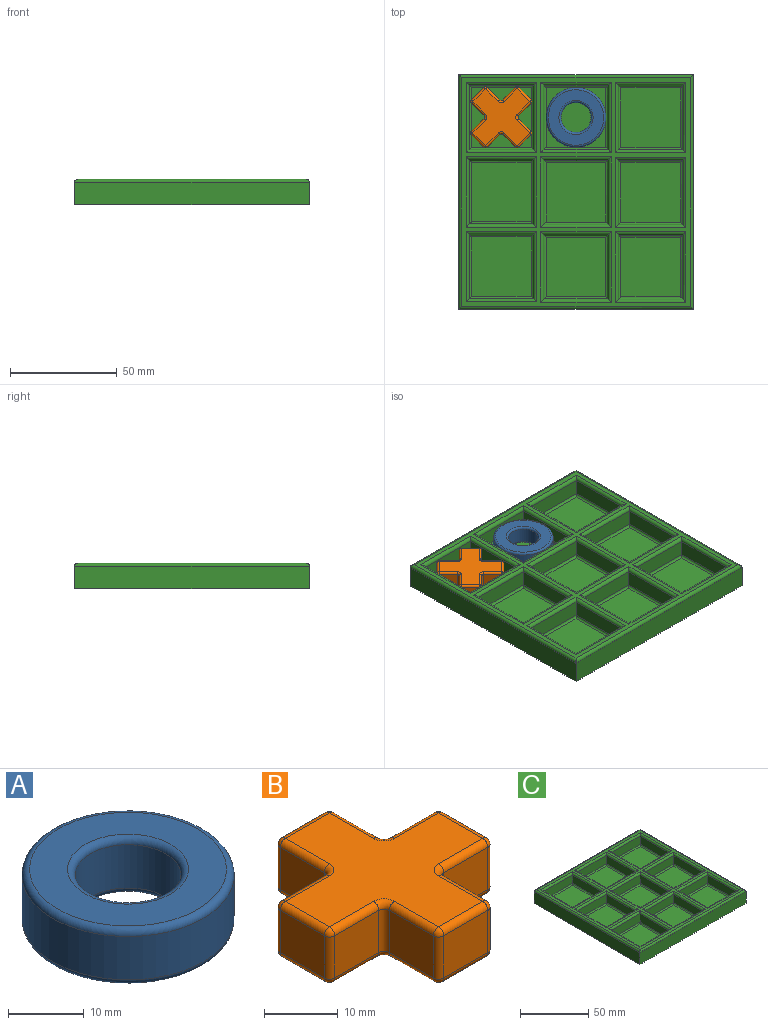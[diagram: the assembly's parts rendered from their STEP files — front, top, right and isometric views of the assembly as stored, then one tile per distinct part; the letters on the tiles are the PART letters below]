
ASSEMBLY  parts=3 mates=2
PART A: 8 faces, bbox 30.3x30.3x9 mm
  f0: cylinder r=7mm len=14mm, axis (0,0,-1), area 307.9mm2, adj f4,f6
  f1: cylinder r=14mm len=28mm, axis (0,0,-1), area 615.8mm2, adj f5,f7
  f2: plane 26x26mm, normal (0,0,1), area 329.9mm2, adj f6,f7
  f3: plane 26x26mm, normal (0,0,-1), area 329.9mm2, adj f4,f5
  f4: torus R=8mm, axis (0,0,1), area 72.7mm2, adj f0,f3
  f5: torus R=13mm, axis (0,0,1), area 134.6mm2, adj f1,f3
  f6: torus R=8mm, axis (0,0,1), area 72.7mm2, adj f0,f2
  f7: torus R=13mm, axis (0,0,1), area 134.6mm2, adj f1,f2
PART B: 74 faces, bbox 31.3x31.3x9 mm
  f0: plane 8.44x7mm, normal (-1,0,0), area 59mm2, adj f62,f67,f70,f73
  f1: plane 8.44x7mm, normal (0,-1,0), area 59mm2, adj f59,f68,f69,f73
  f2: plane 8.44x7mm, normal (1,0,0), area 59mm2, adj f49,f58,f59,f60
  f3: plane 8.44x7mm, normal (0,-1,0), area 59mm2, adj f39,f48,f49,f50
  f4: plane 8.44x7mm, normal (1,0,0), area 59mm2, adj f29,f38,f39,f40
  f5: plane 8.44x7mm, normal (0,1,0), area 59mm2, adj f19,f28,f29,f30
  f6: plane 8.44x7mm, normal (1,0,0), area 59mm2, adj f14,f18,f19,f20
  f7: plane 8.44x7mm, normal (0,1,0), area 59mm2, adj f14,f17,f21,f22
  f8: plane 8.44x7mm, normal (-1,0,0), area 59mm2, adj f22,f27,f31,f32
  f9: plane 8.44x7mm, normal (0,1,0), area 59mm2, adj f32,f37,f41,f42
  f10: plane 8.44x7mm, normal (-1,0,0), area 59mm2, adj f42,f47,f51,f52
  f11: plane 8.44x7mm, normal (0,-1,0), area 59mm2, adj f52,f57,f61,f62
  f12: plane 29.31x29.31mm, normal (0,0,1), area 426.7mm2, adj f17,f18,f24,f27,f28,f33,f37,f38
  f13: plane 29.31x29.31mm, normal (0,0,-1), area 426.7mm2, adj f20,f21,f25,f30,f31,f36,f40,f41
  f14: cylinder r=1mm len=7mm, axis (0,0,1), area 11mm2, adj f6,f7,f15,f16
  f15: sphere r=1mm, area 1.6mm2, adj f14,f17,f18
  f16: sphere r=1mm, area 1.6mm2, adj f14,f20,f21
  f17: cylinder r=1mm len=8.44mm, axis (1,0,0), area 13.3mm2, adj f7,f12,f15,f23
  f18: cylinder r=1mm len=8.44mm, axis (0,-1,0), area 13.3mm2, adj f6,f12,f15,f24
  f19: cylinder r=1mm len=7mm, axis (0,0,-1), area 11mm2, adj f5,f6,f24,f25
  f20: cylinder r=1mm len=8.44mm, axis (0,1,0), area 13.3mm2, adj f6,f13,f16,f25
  f21: cylinder r=1mm len=8.44mm, axis (-1,0,0), area 13.3mm2, adj f7,f13,f16,f26
  f22: cylinder r=1mm len=7mm, axis (0,0,1), area 11mm2, adj f7,f8,f23,f26
  f23: sphere r=1mm, area 1.6mm2, adj f17,f22,f27
  f24: torus R=2mm, axis (0,0,1), area 3.4mm2, adj f12,f18,f19,f28
  f25: torus R=2mm, axis (0,0,1), area 3.4mm2, adj f13,f19,f20,f30
  f26: sphere r=1mm, area 1.6mm2, adj f21,f22,f31
  f27: cylinder r=1mm len=8.44mm, axis (0,1,0), area 13.3mm2, adj f8,f12,f23,f33
  f28: cylinder r=1mm len=8.44mm, axis (1,0,0), area 13.3mm2, adj f5,f12,f24,f34
  f29: cylinder r=1mm len=7mm, axis (0,0,-1), area 11mm2, adj f4,f5,f34,f35
  f30: cylinder r=1mm len=8.44mm, axis (-1,0,0), area 13.3mm2, adj f5,f13,f25,f35
  f31: cylinder r=1mm len=8.44mm, axis (0,-1,0), area 13.3mm2, adj f8,f13,f26,f36
  f32: cylinder r=1mm len=7mm, axis (0,0,-1), area 11mm2, adj f8,f9,f33,f36
  f33: torus R=2mm, axis (0,0,1), area 3.4mm2, adj f12,f27,f32,f37
  f34: sphere r=1mm, area 1.6mm2, adj f28,f29,f38
  f35: sphere r=1mm, area 1.6mm2, adj f29,f30,f40
  f36: torus R=2mm, axis (0,0,1), area 3.4mm2, adj f13,f31,f32,f41
  f37: cylinder r=1mm len=8.44mm, axis (1,0,0), area 13.3mm2, adj f9,f12,f33,f43
  f38: cylinder r=1mm len=8.44mm, axis (0,-1,0), area 13.3mm2, adj f4,f12,f34,f44
  f39: cylinder r=1mm len=7mm, axis (0,0,1), area 11mm2, adj f3,f4,f44,f45
  f40: cylinder r=1mm len=8.44mm, axis (0,1,0), area 13.3mm2, adj f4,f13,f35,f45
  f41: cylinder r=1mm len=8.44mm, axis (-1,0,0), area 13.3mm2, adj f9,f13,f36,f46
  f42: cylinder r=1mm len=7mm, axis (0,0,1), area 11mm2, adj f9,f10,f43,f46
  f43: sphere r=1mm, area 1.6mm2, adj f37,f42,f47
  f44: sphere r=1mm, area 1.6mm2, adj f38,f39,f48
  f45: sphere r=1mm, area 1.6mm2, adj f39,f40,f50
  f46: sphere r=1mm, area 1.6mm2, adj f41,f42,f51
  f47: cylinder r=1mm len=8.44mm, axis (0,1,0), area 13.3mm2, adj f10,f12,f43,f53
  f48: cylinder r=1mm len=8.44mm, axis (-1,0,0), area 13.3mm2, adj f3,f12,f44,f54
  f49: cylinder r=1mm len=7mm, axis (0,0,1), area 11mm2, adj f2,f3,f54,f55
  f50: cylinder r=1mm len=8.44mm, axis (1,0,0), area 13.3mm2, adj f3,f13,f45,f55
  f51: cylinder r=1mm len=8.44mm, axis (0,-1,0), area 13.3mm2, adj f10,f13,f46,f56
  f52: cylinder r=1mm len=7mm, axis (0,0,-1), area 11mm2, adj f10,f11,f53,f56
  f53: sphere r=1mm, area 1.6mm2, adj f47,f52,f57
  f54: torus R=2mm, axis (0,0,1), area 3.4mm2, adj f12,f48,f49,f58
  f55: torus R=2mm, axis (0,0,1), area 3.4mm2, adj f13,f49,f50,f60
  f56: sphere r=1mm, area 1.6mm2, adj f51,f52,f61
  f57: cylinder r=1mm len=8.44mm, axis (-1,0,0), area 13.3mm2, adj f11,f12,f53,f63
  f58: cylinder r=1mm len=8.44mm, axis (0,-1,0), area 13.3mm2, adj f2,f12,f54,f64
  f59: cylinder r=1mm len=7mm, axis (0,0,-1), area 11mm2, adj f1,f2,f64,f65
  f60: cylinder r=1mm len=8.44mm, axis (0,1,0), area 13.3mm2, adj f2,f13,f55,f65
  f61: cylinder r=1mm len=8.44mm, axis (1,0,0), area 13.3mm2, adj f11,f13,f56,f66
  f62: cylinder r=1mm len=7mm, axis (0,0,1), area 11mm2, adj f0,f11,f63,f66
  f63: torus R=2mm, axis (0,0,1), area 3.4mm2, adj f12,f57,f62,f67
  f64: sphere r=1mm, area 1.6mm2, adj f58,f59,f68
  f65: sphere r=1mm, area 1.6mm2, adj f59,f60,f69
  f66: torus R=2mm, axis (0,0,1), area 3.4mm2, adj f13,f61,f62,f70
  f67: cylinder r=1mm len=8.44mm, axis (0,1,0), area 13.3mm2, adj f0,f12,f63,f71
  f68: cylinder r=1mm len=8.44mm, axis (-1,0,0), area 13.3mm2, adj f1,f12,f64,f71
  f69: cylinder r=1mm len=8.44mm, axis (1,0,0), area 13.3mm2, adj f1,f13,f65,f72
  f70: cylinder r=1mm len=8.44mm, axis (0,-1,0), area 13.3mm2, adj f0,f13,f66,f72
  f71: sphere r=1mm, area 1.6mm2, adj f67,f68,f73
  f72: sphere r=1mm, area 1.6mm2, adj f69,f70,f73
  f73: cylinder r=1mm len=7mm, axis (0,0,-1), area 11mm2, adj f0,f1,f71,f72
PART C: 127 faces, bbox 110x110x12 mm
  f0: plane 107x107mm, normal (0,0,1), area 1648mm2, adj f51,f52,f53,f54,f55,f56,f57,f58
  f1: plane 110x10.5mm, normal (0,1,0), area 1155mm2, adj f2,f4,f5,f87
  f2: plane 110x10.5mm, normal (-1,0,0), area 1155mm2, adj f1,f3,f5,f88
  f3: plane 110x10.5mm, normal (0,-1,0), area 1155mm2, adj f2,f4,f5,f90
  f4: plane 110x10.5mm, normal (1,0,0), area 1155mm2, adj f1,f3,f5,f89
  f5: plane 110x110mm, normal (0,0,-1), area 12100mm2, adj f1,f2,f3,f4
  f6: plane 30x7.5mm, normal (0,-1,0), area 225mm2, adj f7,f9,f84,f124
  f7: plane 30x7.5mm, normal (1,0,0), area 225mm2, adj f6,f8,f86,f126
  f8: plane 30x7.5mm, normal (0,1,0), area 225mm2, adj f7,f9,f85,f125
  f9: plane 30x7.5mm, normal (-1,0,0), area 225mm2, adj f6,f8,f83,f123
  f10: plane 28x28mm, normal (0,0,1), area 784mm2, adj f123,f124,f125,f126
  f11: plane 30x7.5mm, normal (0,-1,0), area 225mm2, adj f12,f14,f64,f104
  f12: plane 30x7.5mm, normal (1,0,0), area 225mm2, adj f11,f13,f66,f106
  f13: plane 30x7.5mm, normal (0,1,0), area 225mm2, adj f12,f14,f65,f105
  f14: plane 30x7.5mm, normal (-1,0,0), area 225mm2, adj f11,f13,f63,f103
  f15: plane 28x28mm, normal (0,0,1), area 784mm2, adj f103,f104,f105,f106
  f16: plane 30x7.5mm, normal (0,-1,0), area 225mm2, adj f17,f19,f60,f100
  f17: plane 30x7.5mm, normal (1,0,0), area 225mm2, adj f16,f18,f62,f102
  f18: plane 30x7.5mm, normal (0,1,0), area 225mm2, adj f17,f19,f61,f101
  f19: plane 30x7.5mm, normal (-1,0,0), area 225mm2, adj f16,f18,f59,f99
  f20: plane 28x28mm, normal (0,0,1), area 784mm2, adj f99,f100,f101,f102
  f21: plane 30x7.5mm, normal (0,-1,0), area 225mm2, adj f22,f24,f56,f96
  f22: plane 30x7.5mm, normal (1,0,0), area 225mm2, adj f21,f23,f58,f98
  f23: plane 30x7.5mm, normal (0,1,0), area 225mm2, adj f22,f24,f57,f97
  f24: plane 30x7.5mm, normal (-1,0,0), area 225mm2, adj f21,f23,f55,f95
  f25: plane 28x28mm, normal (0,0,1), area 784mm2, adj f95,f96,f97,f98
  f26: plane 30x7.5mm, normal (0,-1,0), area 225mm2, adj f27,f29,f52,f92
  f27: plane 30x7.5mm, normal (1,0,0), area 225mm2, adj f26,f28,f54,f94
  f28: plane 30x7.5mm, normal (0,1,0), area 225mm2, adj f27,f29,f53,f93
  f29: plane 30x7.5mm, normal (-1,0,0), area 225mm2, adj f26,f28,f51,f91
  f30: plane 28x28mm, normal (0,0,1), area 784mm2, adj f91,f92,f93,f94
  f31: plane 30x7.5mm, normal (0,-1,0), area 225mm2, adj f32,f34,f68,f108
  f32: plane 30x7.5mm, normal (1,0,0), area 225mm2, adj f31,f33,f70,f110
  f33: plane 30x7.5mm, normal (0,1,0), area 225mm2, adj f32,f34,f69,f109
  f34: plane 30x7.5mm, normal (-1,0,0), area 225mm2, adj f31,f33,f67,f107
  f35: plane 28x28mm, normal (0,0,1), area 784mm2, adj f107,f108,f109,f110
  f36: plane 30x7.5mm, normal (0,-1,0), area 225mm2, adj f37,f39,f72,f112
  f37: plane 30x7.5mm, normal (1,0,0), area 225mm2, adj f36,f38,f74,f114
  f38: plane 30x7.5mm, normal (0,1,0), area 225mm2, adj f37,f39,f73,f113
  f39: plane 30x7.5mm, normal (-1,0,0), area 225mm2, adj f36,f38,f71,f111
  f40: plane 28x28mm, normal (0,0,1), area 784mm2, adj f111,f112,f113,f114
  f41: plane 30x7.5mm, normal (0,-1,0), area 225mm2, adj f42,f44,f76,f116
  f42: plane 30x7.5mm, normal (1,0,0), area 225mm2, adj f41,f43,f78,f118
  f43: plane 30x7.5mm, normal (0,1,0), area 225mm2, adj f42,f44,f77,f117
  f44: plane 30x7.5mm, normal (-1,0,0), area 225mm2, adj f41,f43,f75,f115
  f45: plane 28x28mm, normal (0,0,1), area 784mm2, adj f115,f116,f117,f118
  f46: plane 30x7.5mm, normal (0,-1,0), area 225mm2, adj f47,f49,f79,f119
  f47: plane 30x7.5mm, normal (1,0,0), area 225mm2, adj f46,f48,f80,f120
  f48: plane 30x7.5mm, normal (0,1,0), area 225mm2, adj f47,f49,f82,f122
  f49: plane 30x7.5mm, normal (-1,0,0), area 225mm2, adj f46,f48,f81,f121
  f50: plane 28x28mm, normal (0,0,1), area 784mm2, adj f119,f120,f121,f122
  f51: cylinder r=1.5mm len=33mm, axis (0,-1,0), area 73.3mm2, adj f0,f29,f52,f53
  f52: cylinder r=1.5mm len=33mm, axis (1,0,0), area 73.3mm2, adj f0,f26,f51,f54
  f53: cylinder r=1.5mm len=33mm, axis (-1,0,0), area 73.3mm2, adj f0,f28,f51,f54
  f54: cylinder r=1.5mm len=33mm, axis (0,1,0), area 73.3mm2, adj f0,f27,f52,f53
  f55: cylinder r=1.5mm len=33mm, axis (0,-1,0), area 73.3mm2, adj f0,f24,f56,f57
  f56: cylinder r=1.5mm len=33mm, axis (1,0,0), area 73.3mm2, adj f0,f21,f55,f58
  f57: cylinder r=1.5mm len=33mm, axis (-1,0,0), area 73.3mm2, adj f0,f23,f55,f58
  f58: cylinder r=1.5mm len=33mm, axis (0,1,0), area 73.3mm2, adj f0,f22,f56,f57
  f59: cylinder r=1.5mm len=33mm, axis (0,-1,0), area 73.3mm2, adj f0,f19,f60,f61
  f60: cylinder r=1.5mm len=33mm, axis (1,0,0), area 73.3mm2, adj f0,f16,f59,f62
  f61: cylinder r=1.5mm len=33mm, axis (-1,0,0), area 73.3mm2, adj f0,f18,f59,f62
  f62: cylinder r=1.5mm len=33mm, axis (0,1,0), area 73.3mm2, adj f0,f17,f60,f61
  f63: cylinder r=1.5mm len=33mm, axis (0,-1,0), area 73.3mm2, adj f0,f14,f64,f65
  f64: cylinder r=1.5mm len=33mm, axis (1,0,0), area 73.3mm2, adj f0,f11,f63,f66
  f65: cylinder r=1.5mm len=33mm, axis (-1,0,0), area 73.3mm2, adj f0,f13,f63,f66
  f66: cylinder r=1.5mm len=33mm, axis (0,1,0), area 73.3mm2, adj f0,f12,f64,f65
  f67: cylinder r=1.5mm len=33mm, axis (0,-1,0), area 73.3mm2, adj f0,f34,f68,f69
  f68: cylinder r=1.5mm len=33mm, axis (1,0,0), area 73.3mm2, adj f0,f31,f67,f70
  f69: cylinder r=1.5mm len=33mm, axis (-1,0,0), area 73.3mm2, adj f0,f33,f67,f70
  f70: cylinder r=1.5mm len=33mm, axis (0,1,0), area 73.3mm2, adj f0,f32,f68,f69
  f71: cylinder r=1.5mm len=33mm, axis (0,-1,0), area 73.3mm2, adj f0,f39,f72,f73
  f72: cylinder r=1.5mm len=33mm, axis (1,0,0), area 73.3mm2, adj f0,f36,f71,f74
  f73: cylinder r=1.5mm len=33mm, axis (-1,0,0), area 73.3mm2, adj f0,f38,f71,f74
  f74: cylinder r=1.5mm len=33mm, axis (0,1,0), area 73.3mm2, adj f0,f37,f72,f73
  f75: cylinder r=1.5mm len=33mm, axis (0,-1,0), area 73.3mm2, adj f0,f44,f76,f77
  f76: cylinder r=1.5mm len=33mm, axis (1,0,0), area 73.3mm2, adj f0,f41,f75,f78
  f77: cylinder r=1.5mm len=33mm, axis (-1,0,0), area 73.3mm2, adj f0,f43,f75,f78
  f78: cylinder r=1.5mm len=33mm, axis (0,1,0), area 73.3mm2, adj f0,f42,f76,f77
  f79: cylinder r=1.5mm len=33mm, axis (1,0,0), area 73.3mm2, adj f0,f46,f80,f81
  f80: cylinder r=1.5mm len=33mm, axis (0,1,0), area 73.3mm2, adj f0,f47,f79,f82
  f81: cylinder r=1.5mm len=33mm, axis (0,-1,0), area 73.3mm2, adj f0,f49,f79,f82
  f82: cylinder r=1.5mm len=33mm, axis (-1,0,0), area 73.3mm2, adj f0,f48,f80,f81
  f83: cylinder r=1.5mm len=33mm, axis (0,-1,0), area 73.3mm2, adj f0,f9,f84,f85
  f84: cylinder r=1.5mm len=33mm, axis (1,0,0), area 73.3mm2, adj f0,f6,f83,f86
  f85: cylinder r=1.5mm len=33mm, axis (-1,0,0), area 73.3mm2, adj f0,f8,f83,f86
  f86: cylinder r=1.5mm len=33mm, axis (0,1,0), area 73.3mm2, adj f0,f7,f84,f85
  f87: cylinder r=1.5mm len=110mm, axis (1,0,0), area 256.6mm2, adj f0,f1,f88,f89
  f88: cylinder r=1.5mm len=110mm, axis (0,1,0), area 256.6mm2, adj f0,f2,f87,f90
  f89: cylinder r=1.5mm len=110mm, axis (0,-1,0), area 256.6mm2, adj f0,f4,f87,f90
  f90: cylinder r=1.5mm len=110mm, axis (-1,0,0), area 256.6mm2, adj f0,f3,f88,f89
  f91: cylinder r=1mm len=30mm, axis (0,1,0), area 46mm2, adj f29,f30,f92,f93
  f92: cylinder r=1mm len=30mm, axis (-1,0,0), area 46mm2, adj f26,f30,f91,f94
  f93: cylinder r=1mm len=30mm, axis (1,0,0), area 46mm2, adj f28,f30,f91,f94
  f94: cylinder r=1mm len=30mm, axis (0,-1,0), area 46mm2, adj f27,f30,f92,f93
  f95: cylinder r=1mm len=30mm, axis (0,1,0), area 46mm2, adj f24,f25,f96,f97
  f96: cylinder r=1mm len=30mm, axis (-1,0,0), area 46mm2, adj f21,f25,f95,f98
  f97: cylinder r=1mm len=30mm, axis (1,0,0), area 46mm2, adj f23,f25,f95,f98
  f98: cylinder r=1mm len=30mm, axis (0,-1,0), area 46mm2, adj f22,f25,f96,f97
  f99: cylinder r=1mm len=30mm, axis (0,1,0), area 46mm2, adj f19,f20,f100,f101
  f100: cylinder r=1mm len=30mm, axis (-1,0,0), area 46mm2, adj f16,f20,f99,f102
  f101: cylinder r=1mm len=30mm, axis (1,0,0), area 46mm2, adj f18,f20,f99,f102
  f102: cylinder r=1mm len=30mm, axis (0,-1,0), area 46mm2, adj f17,f20,f100,f101
  f103: cylinder r=1mm len=30mm, axis (0,1,0), area 46mm2, adj f14,f15,f104,f105
  f104: cylinder r=1mm len=30mm, axis (-1,0,0), area 46mm2, adj f11,f15,f103,f106
  f105: cylinder r=1mm len=30mm, axis (1,0,0), area 46mm2, adj f13,f15,f103,f106
  f106: cylinder r=1mm len=30mm, axis (0,-1,0), area 46mm2, adj f12,f15,f104,f105
  f107: cylinder r=1mm len=30mm, axis (0,1,0), area 46mm2, adj f34,f35,f108,f109
  f108: cylinder r=1mm len=30mm, axis (-1,0,0), area 46mm2, adj f31,f35,f107,f110
  f109: cylinder r=1mm len=30mm, axis (1,0,0), area 46mm2, adj f33,f35,f107,f110
  f110: cylinder r=1mm len=30mm, axis (0,-1,0), area 46mm2, adj f32,f35,f108,f109
  f111: cylinder r=1mm len=30mm, axis (0,1,0), area 46mm2, adj f39,f40,f112,f113
  f112: cylinder r=1mm len=30mm, axis (-1,0,0), area 46mm2, adj f36,f40,f111,f114
  f113: cylinder r=1mm len=30mm, axis (1,0,0), area 46mm2, adj f38,f40,f111,f114
  f114: cylinder r=1mm len=30mm, axis (0,-1,0), area 46mm2, adj f37,f40,f112,f113
  f115: cylinder r=1mm len=30mm, axis (0,1,0), area 46mm2, adj f44,f45,f116,f117
  f116: cylinder r=1mm len=30mm, axis (-1,0,0), area 46mm2, adj f41,f45,f115,f118
  f117: cylinder r=1mm len=30mm, axis (1,0,0), area 46mm2, adj f43,f45,f115,f118
  f118: cylinder r=1mm len=30mm, axis (0,-1,0), area 46mm2, adj f42,f45,f116,f117
  f119: cylinder r=1mm len=30mm, axis (-1,0,0), area 46mm2, adj f46,f50,f120,f121
  f120: cylinder r=1mm len=30mm, axis (0,-1,0), area 46mm2, adj f47,f50,f119,f122
  f121: cylinder r=1mm len=30mm, axis (0,1,0), area 46mm2, adj f49,f50,f119,f122
  f122: cylinder r=1mm len=30mm, axis (1,0,0), area 46mm2, adj f48,f50,f120,f121
  f123: cylinder r=1mm len=30mm, axis (0,1,0), area 46mm2, adj f9,f10,f124,f125
  f124: cylinder r=1mm len=30mm, axis (-1,0,0), area 46mm2, adj f6,f10,f123,f126
  f125: cylinder r=1mm len=30mm, axis (1,0,0), area 46mm2, adj f8,f10,f123,f126
  f126: cylinder r=1mm len=30mm, axis (0,-1,0), area 46mm2, adj f7,f10,f124,f125
PLACE A t=(131.21,14.31,-6.9)mm
PLACE B rot(axis=(0,0,1),45deg) t=(92.88,10.36,-6.9)mm
PLACE C t=(130.52,-21.98,-8.9)mm
MATE cylindrical A.f1 <-> C.f40  axis (0,0,-1) through (131.21,14.31,-6.9)mm
MATE cylindrical C.f10 <-> B.f13  axis (0,0,1) through (96.21,14.41,-6.9)mm
